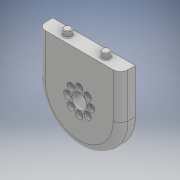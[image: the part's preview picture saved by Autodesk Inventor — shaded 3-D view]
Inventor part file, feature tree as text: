
AUTODESK INVENTOR PART (.ipt)
format: ipt  version: 2018 (Build 220112000, 112)  size: 451,072 bytes
history: native  units: mm
features: sketch x5, extrude x4, fillet x2, projected_geometry x2, hole x1
ambient origin geometry x8: Origin, YZ Plane, XZ Plane, XY Plane, X Axis, Y Axis, Z Axis, Center Point
bodies: Solid1 (feature_tree)
feature tree (14):
  extrude  "Extrusion1"  Depth=28.0mm
  extrude  "Extrusion2"  TaperAngle=90.0deg  [1 undecoded]
  hole  "Hole1"  [1 undecoded]
  extrude  "Extrusion6"  Depth=4.0mm
  extrude  "Extrusion7"  Depth=10.0mm
  fillet  "Fillet4"  Radius=5.0mm
  fillet  "Fillet5"  Radius=5.0mm
  sketch  "Sketch1"  dims[d1=80.0mm d2=1.0mm d3=10.0mm d4=16.0mm d5=2.9mm d6=360.0deg d7=28.0mm]
  sketch  "Sketch2"  dims[d8=34.0mm d9=90.0deg]
  projected_geometry  "Projected Loop1"
  sketch  "Sketch3"  dims[d10=10.0mm d11=0.0mm d12=4.5mm d13=0.0mm]
  projected_geometry  "Projected Loop2"
  sketch  "Sketch4"  dims[d14=5.0mm d15=6.0mm d16=4.0mm d17=2.0mm d18=90.0deg d19=10.5mm d20=0.0mm d21=4.0mm]
  sketch  "Sketch9"  dims[d62=10.0mm d63=0.0mm d64=10.0mm d65=15.0mm d66=15.0mm d67=5.0mm d68=5.0mm d69=4.0mm d70=0.0mm d71=0.5mm d72=5.0mm]
note: 2 required parameter values undecoded (feature->parameter linkage not recoverable at this tier; creation-order binding heuristic only, values carry confidence <= 0.55)
